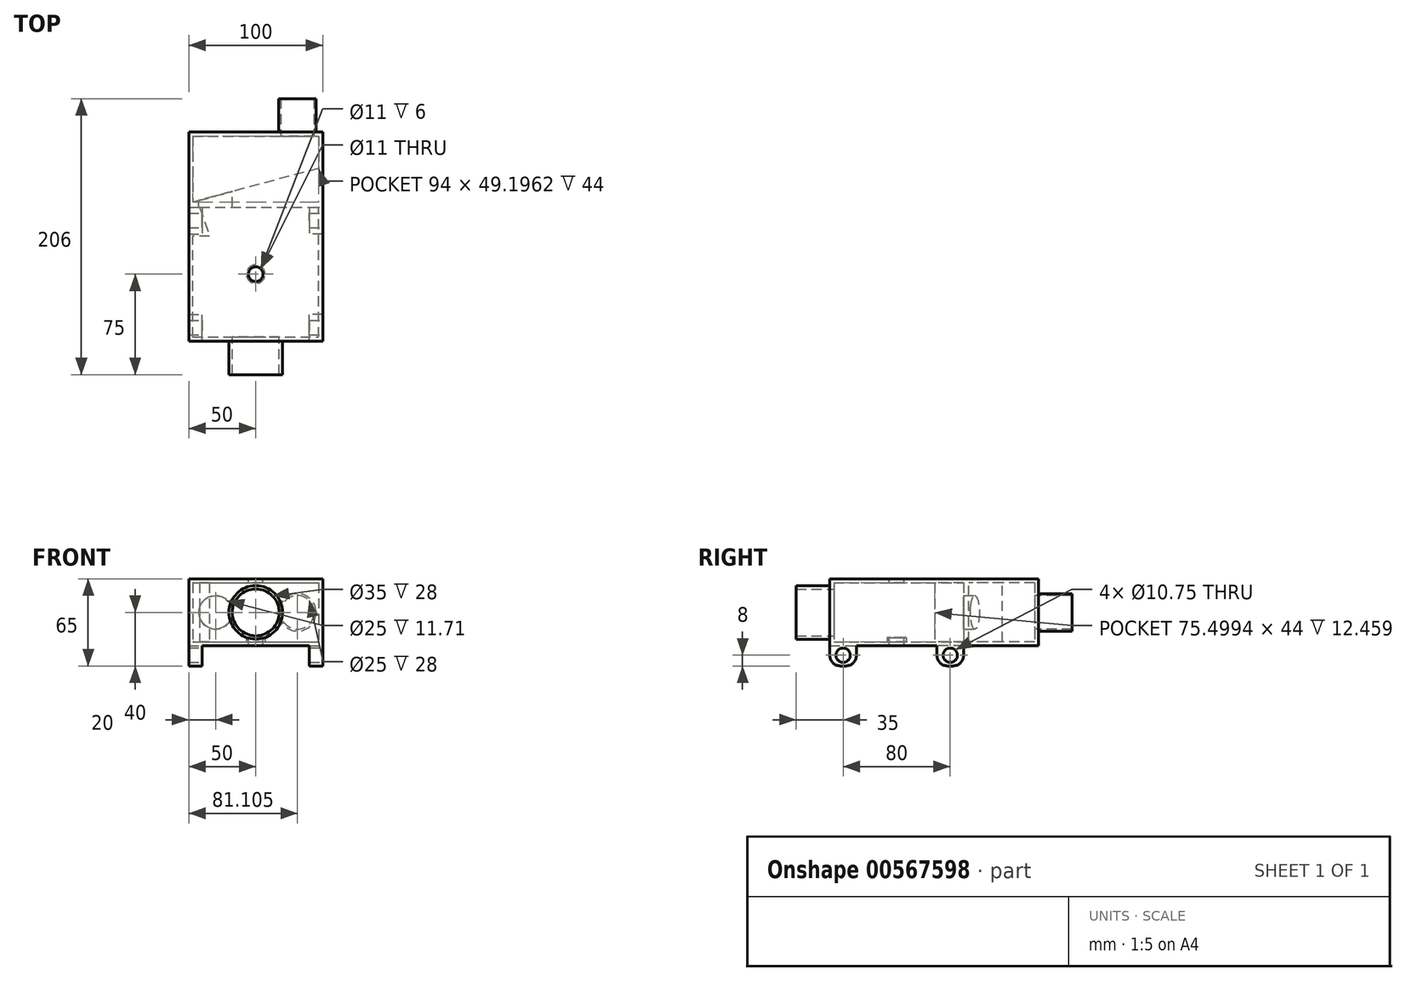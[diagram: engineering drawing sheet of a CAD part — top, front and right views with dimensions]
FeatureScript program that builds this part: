
annotation { "Feature Type Name" : "Feature", "Feature Type Description" : "" }
export const myFeature = defineFeature(function(context is Context, id is Id, definition is map)
    precondition{}
    {
        {
            var Q0;
            Q0=qCreatedBy(makeId("Top.planeOp"),FACE);
            var sketch = newSketch(context, id + "F0", { "sketchPlane" : qUnion([Q0])});
            skLineSegment(sketch, "E0.bottom", {"start": v(-50, -50) * mm, "end": v(50, -50) * mm});
            skLineSegment(sketch, "E0.top", {"start": v(-50, 50) * mm, "end": v(50, 50) * mm});
            skLineSegment(sketch, "E0.left", {"start": v(-50, -50) * mm, "end": v(-50, 50) * mm});
            skLineSegment(sketch, "E0.right", {"start": v(50, -50) * mm, "end": v(50, 50) * mm});
            skPoint(sketch, "E0.middle", {"position": v(0, 0) * mm});
            skSolve(sketch);
        }
        {
            var Q0;
            Q0 = qSketchRegion(id + "F0", true);
            extrude(context, id + "F1", {"entities" : qUnion([Q0]), "depth" : 50 * mm, "offsetDistance" : 25 * mm});
        }
        {
            var Q0;
            Q0=makeQuery(id+"F1.opExtrude","SWEPT_FACE",FACE,{"disambiguationData":[OSD([sQuery(id+"F0.wireOp",EDGE,"E0.top")])]});
            shell(context, id + "F2", {"entities" : qUnion([Q0]), "thickness" : 3 * mm});
        }
        {
            var Q0;
            Q0=makeQuery(id+"F1.opExtrude","CAP_FACE",FACE,{"disambiguationData":[OSD([sQuery(id+"F0.wireOp",EDGE,"E0.bottom"),sQuery(id+"F0.wireOp",EDGE,"E0.top"),sQuery(id+"F0.wireOp",EDGE,"E0.left"),sQuery(id+"F0.wireOp",EDGE,"E0.right")])],"isStart":false});
            var sketch = newSketch(context, id + "F3", { "sketchPlane" : qUnion([Q0])});
            skCircle(sketch, "E1", {"center": v(0, 0) * mm, "radius": 5.5 * mm});
            skSolve(sketch);
        }
        {
            var Q0;
            Q0 = qSketchRegion(id + "F3", true);
            var Q1;
            Q1=makeQuery(id+"F1.opExtrude","CAP_FACE",FACE,{"disambiguationData":[OSD([sQuery(id+"F0.wireOp",EDGE,"E0.bottom"),sQuery(id+"F0.wireOp",EDGE,"E0.top"),sQuery(id+"F0.wireOp",EDGE,"E0.left"),sQuery(id+"F0.wireOp",EDGE,"E0.right")])],"isStart":true});
            extrude(context, id + "F4", {"entities" : qUnion([Q0]), "operationType" : NewBodyOperationType.REMOVE, "endBound" : BoundingType.UP_TO_SURFACE, "oppositeDirection" : true, "depth" : 25 * mm, "endBoundEntityFace" : qUnion([Q1]), "offsetDistance" : 25 * mm});
        }
        {
            var Q0;
            Q0=makeQuery(id+"F1.opExtrude","SWEPT_FACE",FACE,{"disambiguationData":[OSD([sQuery(id+"F0.wireOp",EDGE,"E0.bottom")])]});
            var sketch = newSketch(context, id + "F5", { "sketchPlane" : qUnion([Q0])});
            skCircle(sketch, "E2", {"center": v(0, 25) * mm, "radius": 17.5 * mm});
            skPoint(sketch, "E2.centerSnap0", {"position": v(-50, 25) * mm});
            skPoint(sketch, "E2.centerSnap1", {"position": v(0, 0) * mm});
            skCircle(sketch, "E3", {"center": v(0, 25) * mm, "radius": 20 * mm});
            skSolve(sketch);
        }
        {
            var Q0;
            Q0=makeQuery(id+"F5.imprint","IMPRINT",FACE,{"disambiguationData":[TD([[makeQuery(id+"F5.imprint","IMPRINT",EDGE,{"derivedFrom":sQuery(id+"F5.wireOp",EDGE,"E2")}),-1.0]])]});
            extrude(context, id + "F6", {"entities" : qUnion([Q0]), "operationType" : NewBodyOperationType.ADD, "depth" : 25 * mm, "offsetDistance" : 25 * mm});
        }
        {
            var Q0;
            Q0=makeQuery(id+"F5.imprint","IMPRINT",FACE,{"disambiguationData":[TD([[makeQuery(id+"F5.imprint","IMPRINT",EDGE,{"derivedFrom":sQuery(id+"F5.wireOp",EDGE,"E2")}),1.0]])]});
            extrude(context, id + "F7", {"entities" : qUnion([Q0]), "operationType" : NewBodyOperationType.REMOVE, "endBound" : BoundingType.UP_TO_NEXT, "oppositeDirection" : true, "depth" : 25 * mm, "offsetDistance" : 25 * mm});
        }
        {
            var Q0;
            Q0=makeQuery(id+"F1.opExtrude","CAP_FACE",FACE,{"disambiguationData":[OSD([sQuery(id+"F0.wireOp",EDGE,"E0.bottom"),sQuery(id+"F0.wireOp",EDGE,"E0.top"),sQuery(id+"F0.wireOp",EDGE,"E0.left"),sQuery(id+"F0.wireOp",EDGE,"E0.right")])],"isStart":true});
            var sketch = newSketch(context, id + "F8", { "sketchPlane" : qUnion([Q0])});
            skLineSegment(sketch, "E4.bottom", {"start": v(50, -50) * mm, "end": v(40, -50) * mm});
            skLineSegment(sketch, "E4.top", {"start": v(50, -30) * mm, "end": v(40, -30) * mm});
            skLineSegment(sketch, "E4.left", {"start": v(50, -50) * mm, "end": v(50, -30) * mm});
            skLineSegment(sketch, "E4.right", {"start": v(40, -50) * mm, "end": v(40, -30) * mm});
            skLineSegment(sketch, "E5.bottom", {"start": v(-50, -50) * mm, "end": v(-40, -50) * mm});
            skLineSegment(sketch, "E5.top", {"start": v(-50, -30) * mm, "end": v(-40, -30) * mm});
            skLineSegment(sketch, "E5.left", {"start": v(-50, -50) * mm, "end": v(-50, -30) * mm});
            skLineSegment(sketch, "E5.right", {"start": v(-40, -50) * mm, "end": v(-40, -30) * mm});
            skLineSegment(sketch, "E6.bottom", {"start": v(-50, 50) * mm, "end": v(-40, 50) * mm});
            skLineSegment(sketch, "E6.top", {"start": v(-50, 30) * mm, "end": v(-40, 30) * mm});
            skLineSegment(sketch, "E6.left", {"start": v(-50, 50) * mm, "end": v(-50, 30) * mm});
            skLineSegment(sketch, "E6.right", {"start": v(-40, 50) * mm, "end": v(-40, 30) * mm});
            skLineSegment(sketch, "E7.bottom", {"start": v(50, 50) * mm, "end": v(40, 50) * mm});
            skLineSegment(sketch, "E7.top", {"start": v(50, 30) * mm, "end": v(40, 30) * mm});
            skLineSegment(sketch, "E7.left", {"start": v(50, 50) * mm, "end": v(50, 30) * mm});
            skLineSegment(sketch, "E7.right", {"start": v(40, 50) * mm, "end": v(40, 30) * mm});
            skSolve(sketch);
        }
        {
            var Q0;
            Q0 = qSketchRegion(id + "F8", true);
            extrude(context, id + "F9", {"entities" : qUnion([Q0]), "operationType" : NewBodyOperationType.ADD, "depth" : 15 * mm, "offsetDistance" : 25 * mm});
        }
        {
            var Q0;
            Q0=makeQuery(id+"F9.boolean.opBoolean","MERGE",FACE,{"derivedFrom":[makeQuery(id+"F1.opExtrude","SWEPT_FACE",FACE,{"disambiguationData":[OSD([sQuery(id+"F0.wireOp",EDGE,"E0.right")])]}),makeQuery(id+"F9.opExtrude","SWEPT_FACE",FACE,{"disambiguationData":[OSD([sQuery(id+"F8.wireOp",EDGE,"E4.left")])]}),makeQuery(id+"F9.opExtrude","SWEPT_FACE",FACE,{"disambiguationData":[OSD([sQuery(id+"F8.wireOp",EDGE,"E7.left")])]})]});
            var sketch = newSketch(context, id + "F10", { "sketchPlane" : qUnion([Q0])});
            skCircle(sketch, "E8", {"center": v(40, -7) * mm, "radius": 5.37 * mm});
            skPoint(sketch, "E8.centerSnap0", {"position": v(40, -15) * mm});
            skCircle(sketch, "E9", {"center": v(-40, -7) * mm, "radius": 5.37 * mm});
            skPoint(sketch, "E9.centerSnap0", {"position": v(-40, -15) * mm});
            skSolve(sketch);
        }
        {
            var Q0;
            Q0 = qSketchRegion(id + "F10", true);
            var Q1;
            Q1=makeQuery(id+"F9.boolean.opBoolean","MERGE",FACE,{"derivedFrom":[makeQuery(id+"F1.opExtrude","SWEPT_FACE",FACE,{"disambiguationData":[OSD([sQuery(id+"F0.wireOp",EDGE,"E0.left")])]}),makeQuery(id+"F9.opExtrude","SWEPT_FACE",FACE,{"disambiguationData":[OSD([sQuery(id+"F8.wireOp",EDGE,"E5.left")])]}),makeQuery(id+"F9.opExtrude","SWEPT_FACE",FACE,{"disambiguationData":[OSD([sQuery(id+"F8.wireOp",EDGE,"E6.left")])]})]});
            extrude(context, id + "F11", {"entities" : qUnion([Q0]), "operationType" : NewBodyOperationType.REMOVE, "endBound" : BoundingType.UP_TO_SURFACE, "oppositeDirection" : true, "depth" : 25 * mm, "endBoundEntityFace" : qUnion([Q1]), "offsetDistance" : 25 * mm});
        }
        {
            var Q0;
            Q0=makeQuery(id+"F9.opExtrude","CAP_EDGE",EDGE,{"disambiguationData":[OSD([sQuery(id+"F8.wireOp",EDGE,"E4.top")])],"isStart":false});
            var Q1;
            Q1=makeQuery(id+"F9.opExtrude","CAP_EDGE",EDGE,{"disambiguationData":[OSD([sQuery(id+"F8.wireOp",EDGE,"E4.bottom")])],"isStart":false});
            var Q2;
            Q2=makeQuery(id+"F9.opExtrude","CAP_EDGE",EDGE,{"disambiguationData":[OSD([sQuery(id+"F8.wireOp",EDGE,"E5.bottom")])],"isStart":false});
            var Q3;
            Q3=makeQuery(id+"F9.opExtrude","CAP_EDGE",EDGE,{"disambiguationData":[OSD([sQuery(id+"F8.wireOp",EDGE,"E5.top")])],"isStart":false});
            var Q4;
            Q4=makeQuery(id+"F9.opExtrude","CAP_EDGE",EDGE,{"disambiguationData":[OSD([sQuery(id+"F8.wireOp",EDGE,"E7.bottom")])],"isStart":false});
            var Q5;
            Q5=makeQuery(id+"F9.opExtrude","CAP_EDGE",EDGE,{"disambiguationData":[OSD([sQuery(id+"F8.wireOp",EDGE,"E7.top")])],"isStart":false});
            var Q6;
            Q6=makeQuery(id+"F9.opExtrude","CAP_EDGE",EDGE,{"disambiguationData":[OSD([sQuery(id+"F8.wireOp",EDGE,"E6.bottom")])],"isStart":false});
            var Q7;
            Q7=makeQuery(id+"F9.opExtrude","CAP_EDGE",EDGE,{"disambiguationData":[OSD([sQuery(id+"F8.wireOp",EDGE,"E6.top")])],"isStart":false});
            fillet(context, id + "F12", {"entities" : qUnion([Q0, Q1, Q2, Q3, Q4, Q5, Q6, Q7]), "radius" : 8 * mm, "tangentPropagation" : true, "allowEdgeOverflow" : false});
        }
        {
            var Q0;
            {var subQ0=sQuery(id+"F0.wireOp",EDGE,"E0.right");var subQ1=sQuery(id+"F0.wireOp",EDGE,"E0.left");var subQ2=sQuery(id+"F0.wireOp",EDGE,"E0.top");var subQ3=sQuery(id+"F0.wireOp",EDGE,"E0.bottom");Q0=makeQuery(id+"F2.opShell","OFFSET_FACE",FACE,{"disambiguationData":[OSD([subQ3,subQ2,subQ1,subQ0]),TDD([makeQuery(id+"F1.opExtrude","CAP_FACE",FACE,{"disambiguationData":[OSD([subQ3,subQ2,subQ1,subQ0])],"isStart":true})])]});}
            var sketch = newSketch(context, id + "F13", { "sketchPlane" : qUnion([Q0])});
            skCircle(sketch, "E10", {"center": v(0, 0) * mm, "radius": 7 * mm});
            skSolve(sketch);
        }
        {
            var Q0;
            Q0=makeQuery(id+"F13.imprint","IMPRINT",FACE,{"disambiguationData":[TD([[makeQuery(id+"F13.imprint","IMPRINT",EDGE,{"derivedFrom":sQuery(id+"F13.wireOp",EDGE,"E10")}),1.0]])]});
            extrude(context, id + "F14", {"entities" : qUnion([Q0]), "operationType" : NewBodyOperationType.ADD, "depth" : 3 * mm, "offsetDistance" : 25 * mm});
        }
        {
            var Q0;
            Q0=makeQuery(id+"F9.boolean.opBoolean","MERGE",FACE,{"derivedFrom":[makeQuery(id+"F1.opExtrude","SWEPT_FACE",FACE,{"disambiguationData":[OSD([sQuery(id+"F0.wireOp",EDGE,"E0.top")])]}),makeQuery(id+"F9.opExtrude","SWEPT_FACE",FACE,{"disambiguationData":[OSD([sQuery(id+"F8.wireOp",EDGE,"E4.bottom")])]}),makeQuery(id+"F9.opExtrude","SWEPT_FACE",FACE,{"disambiguationData":[OSD([sQuery(id+"F8.wireOp",EDGE,"E5.bottom")])]})]});
            var sketch = newSketch(context, id + "F15", { "sketchPlane" : qUnion([Q0])});
            skLineSegment(sketch, "E11.bottom", {"start": v(50, 50) * mm, "end": v(-50, 50) * mm});
            skLineSegment(sketch, "E11.top", {"start": v(50, 0) * mm, "end": v(-50, 0) * mm});
            skLineSegment(sketch, "E11.left", {"start": v(50, 50) * mm, "end": v(50, 0) * mm});
            skLineSegment(sketch, "E11.right", {"start": v(-50, 50) * mm, "end": v(-50, 0) * mm});
            skSolve(sketch);
        }
        {
            var Q0;
            Q0 = qSketchRegion(id + "F15", true);
            extrude(context, id + "F16", {"entities" : qUnion([Q0]), "operationType" : NewBodyOperationType.ADD, "depth" : 3 * mm, "offsetDistance" : 25 * mm});
        }
        {
            var Q0;
            Q0=qCreatedBy(makeId("Top.planeOp"),FACE);
            var sketch = newSketch(context, id + "F17", { "sketchPlane" : qUnion([Q0])});
            skLineSegment(sketch, "E12", {"start": v(50, 53) * mm, "end": v(-50, 53) * mm});
            skLineSegment(sketch, "E13", {"start": v(-50, 53) * mm, "end": v(50, 79.8) * mm});
            skLineSegment(sketch, "E14", {"start": v(50, 79.8) * mm, "end": v(50, 53) * mm});
            skSolve(sketch);
        }
        {
            var Q0;
            Q0 = qSketchRegion(id + "F17", true);
            var Q1;
            Q1=makeQuery(id+"F16.boolean.opBoolean","MERGE",FACE,{"derivedFrom":[makeQuery(id+"F1.opExtrude","CAP_FACE",FACE,{"disambiguationData":[OSD([sQuery(id+"F0.wireOp",EDGE,"E0.bottom"),sQuery(id+"F0.wireOp",EDGE,"E0.top"),sQuery(id+"F0.wireOp",EDGE,"E0.left"),sQuery(id+"F0.wireOp",EDGE,"E0.right")])],"isStart":false}),makeQuery(id+"F16.opExtrude","SWEPT_FACE",FACE,{"disambiguationData":[OSD([sQuery(id+"F15.wireOp",EDGE,"E11.bottom")])]})]});
            extrude(context, id + "F18", {"entities" : qUnion([Q0]), "operationType" : NewBodyOperationType.ADD, "endBound" : BoundingType.UP_TO_SURFACE, "depth" : 25 * mm, "endBoundEntityFace" : qUnion([Q1]), "offsetDistance" : 25 * mm});
        }
        {
            var Q0;
            Q0=makeQuery(id+"F16.boolean.opBoolean","MERGE",EDGE,{"derivedFrom":[makeQuery(id+"F1.opExtrude","CAP_EDGE",EDGE,{"disambiguationData":[OSD([sQuery(id+"F0.wireOp",EDGE,"E0.left")])],"isStart":false}),makeQuery(id+"F16.opExtrude","SWEPT_EDGE",EDGE,{"disambiguationData":[OSD([sQuery(id+"F15.wireOp",EDGE,"E11.bottom"),sQuery(id+"F15.wireOp",EDGE,"E11.left")])]})]});
            var Q1;
            {var subQ0=sQuery(id+"F15.wireOp",EDGE,"E11.bottom");Q1=makeQuery(id+"F18.boolean.opBoolean","MERGE",VERTEX,{"derivedFrom":[makeQuery(id+"F16.opExtrude","CAP_VERTEX",VERTEX,{"disambiguationData":[OSD([subQ0,sQuery(id+"F15.wireOp",EDGE,"E11.left")])],"isStart":false}),makeQuery(id+"F18.opExtrude","CAP_VERTEX",VERTEX,{"disambiguationData":[OSD([sQuery(id+"F0.wireOp",EDGE,"E0.bottom"),sQuery(id+"F0.wireOp",EDGE,"E0.top"),sQuery(id+"F0.wireOp",EDGE,"E0.left"),sQuery(id+"F0.wireOp",EDGE,"E0.right"),subQ0,sQuery(id+"F17.wireOp",EDGE,"E12"),sQuery(id+"F17.wireOp",EDGE,"E13")])],"isStart":false})]});}
            cPlane(context, id + "F19", {"entities" : qUnion([Q0, Q1]), "cplaneType" : CPlaneType.CURVE_POINT, "offset" : 25 * mm, "width" : 150 * mm, "height" : 150 * mm});
        }
        {
            var Q0;
            Q0=qCreatedBy(id+"F19.planeOp",FACE);
            var sketch = newSketch(context, id + "F20", { "sketchPlane" : qUnion([Q0])});
            skLineSegment(sketch, "E15.bottom", {"start": v(50, 50) * mm, "end": v(-50, 50) * mm});
            skLineSegment(sketch, "E15.top", {"start": v(50, 0) * mm, "end": v(-50, 0) * mm});
            skLineSegment(sketch, "E15.left", {"start": v(50, 50) * mm, "end": v(50, 0) * mm});
            skLineSegment(sketch, "E15.right", {"start": v(-50, 50) * mm, "end": v(-50, 0) * mm});
            skLineSegment(sketch, "E16.0", {"start": v(-47, 47) * mm, "end": v(-47, 3) * mm});
            skLineSegment(sketch, "E16.1", {"start": v(47, 47) * mm, "end": v(-47, 47) * mm});
            skLineSegment(sketch, "E16.2", {"start": v(47, 47) * mm, "end": v(47, 3) * mm});
            skLineSegment(sketch, "E16.3", {"start": v(47, 3) * mm, "end": v(-47, 3) * mm});
            skSolve(sketch);
        }
        {
            var Q0;
            Q0 = qSketchRegion(id + "F20", true);
            extrude(context, id + "F21", {"entities" : qUnion([Q0]), "operationType" : NewBodyOperationType.ADD, "depth" : 50 * mm, "offsetDistance" : 25 * mm});
        }
        {
            var Q0;
            Q0=makeQuery(id+"F21.opExtrude","CAP_FACE",FACE,{"disambiguationData":[OSD([sQuery(id+"F20.wireOp",EDGE,"E15.bottom"),sQuery(id+"F20.wireOp",EDGE,"E15.top"),sQuery(id+"F20.wireOp",EDGE,"E15.left"),sQuery(id+"F20.wireOp",EDGE,"E15.right"),sQuery(id+"F20.wireOp",EDGE,"E16.0"),sQuery(id+"F20.wireOp",EDGE,"E16.1"),sQuery(id+"F20.wireOp",EDGE,"E16.2"),sQuery(id+"F20.wireOp",EDGE,"E16.3")])],"isStart":false});
            var sketch = newSketch(context, id + "F22", { "sketchPlane" : qUnion([Q0])});
            skCircle(sketch, "E17", {"center": v(30, 25) * mm, "radius": 12.5 * mm});
            skPoint(sketch, "E17.centerSnap0", {"position": v(50, 25) * mm});
            skSolve(sketch);
        }
        {
            var Q0;
            Q0=makeQuery(id+"F22.imprint","IMPRINT",FACE,{"disambiguationData":[TD([[makeQuery(id+"F22.imprint","IMPRINT",EDGE,{"derivedFrom":sQuery(id+"F22.wireOp",EDGE,"E17")}),1.0]])]});
            var Q1;
            Q1=makeQuery(id+"F16.opExtrude","CAP_FACE",FACE,{"disambiguationData":[OSD([sQuery(id+"F15.wireOp",EDGE,"E11.bottom"),sQuery(id+"F15.wireOp",EDGE,"E11.top"),sQuery(id+"F15.wireOp",EDGE,"E11.left"),sQuery(id+"F15.wireOp",EDGE,"E11.right")])],"isStart":true});
            extrude(context, id + "F23", {"entities" : qUnion([Q0]), "operationType" : NewBodyOperationType.REMOVE, "endBound" : BoundingType.UP_TO_SURFACE, "oppositeDirection" : true, "depth" : 25 * mm, "endBoundEntityFace" : qUnion([Q1]), "offsetDistance" : 25 * mm});
        }
        {
            var Q0;
            Q0=makeQuery(id+"F21.opExtrude","CAP_FACE",FACE,{"disambiguationData":[OSD([sQuery(id+"F20.wireOp",EDGE,"E15.bottom"),sQuery(id+"F20.wireOp",EDGE,"E15.top"),sQuery(id+"F20.wireOp",EDGE,"E15.left"),sQuery(id+"F20.wireOp",EDGE,"E15.right"),sQuery(id+"F20.wireOp",EDGE,"E16.0"),sQuery(id+"F20.wireOp",EDGE,"E16.1"),sQuery(id+"F20.wireOp",EDGE,"E16.2"),sQuery(id+"F20.wireOp",EDGE,"E16.3")])],"isStart":false});
            var sketch = newSketch(context, id + "F24", { "sketchPlane" : qUnion([Q0])});
            skLineSegment(sketch, "E18.bottom", {"start": v(50, 0) * mm, "end": v(-50, 0) * mm});
            skLineSegment(sketch, "E18.top", {"start": v(50, 50) * mm, "end": v(-50, 50) * mm});
            skLineSegment(sketch, "E18.left", {"start": v(50, 0) * mm, "end": v(50, 50) * mm});
            skLineSegment(sketch, "E18.right", {"start": v(-50, 0) * mm, "end": v(-50, 50) * mm});
            skSolve(sketch);
        }
        {
            var Q0;
            Q0 = qSketchRegion(id + "F24", true);
            extrude(context, id + "F25", {"entities" : qUnion([Q0]), "operationType" : NewBodyOperationType.ADD, "depth" : 3 * mm, "offsetDistance" : 25 * mm});
        }
        {
            var Q0;
            Q0=makeQuery(id+"F25.opExtrude","CAP_FACE",FACE,{"disambiguationData":[OSD([sQuery(id+"F24.wireOp",EDGE,"E18.bottom"),sQuery(id+"F24.wireOp",EDGE,"E18.top"),sQuery(id+"F24.wireOp",EDGE,"E18.left"),sQuery(id+"F24.wireOp",EDGE,"E18.right")])],"isStart":false});
            var sketch = newSketch(context, id + "F26", { "sketchPlane" : qUnion([Q0])});
            skCircle(sketch, "E19", {"center": v(-31.1, 25) * mm, "radius": 12.5 * mm});
            skPoint(sketch, "E19.centerSnap0", {"position": v(-50, 25) * mm});
            skCircle(sketch, "E20", {"center": v(-31.1, 25) * mm, "radius": 14 * mm});
            skSolve(sketch);
        }
        {
            var Q0;
            Q0=makeQuery(id+"F26.imprint","IMPRINT",FACE,{"disambiguationData":[TD([[makeQuery(id+"F26.imprint","IMPRINT",EDGE,{"derivedFrom":sQuery(id+"F26.wireOp",EDGE,"E19")}),-1.0]])]});
            extrude(context, id + "F27", {"entities" : qUnion([Q0]), "operationType" : NewBodyOperationType.ADD, "depth" : 25 * mm, "offsetDistance" : 25 * mm});
        }
        {
            var Q0;
            Q0=makeQuery(id+"F27.boolean.opBoolean","SPLIT",FACE,{"disambiguationData":[TD([makeQuery(id+"F27.opExtrude","SWEPT_FACE",FACE,{"disambiguationData":[OSD([sQuery(id+"F26.wireOp",EDGE,"E19")])]})])],"derivedFrom":makeQuery(id+"F25.opExtrude","CAP_FACE",FACE,{"disambiguationData":[OSD([sQuery(id+"F24.wireOp",EDGE,"E18.bottom"),sQuery(id+"F24.wireOp",EDGE,"E18.top"),sQuery(id+"F24.wireOp",EDGE,"E18.left"),sQuery(id+"F24.wireOp",EDGE,"E18.right")])],"isStart":false})});
            extrude(context, id + "F28", {"entities" : qUnion([Q0]), "operationType" : NewBodyOperationType.REMOVE, "endBound" : BoundingType.UP_TO_NEXT, "oppositeDirection" : true, "depth" : 25 * mm, "offsetDistance" : 25 * mm});
        }
        {
            var Q0;
            {var subQ0=sQuery(id+"F0.wireOp",EDGE,"E0.right");var subQ1=sQuery(id+"F0.wireOp",EDGE,"E0.left");var subQ2=sQuery(id+"F0.wireOp",EDGE,"E0.top");var subQ3=sQuery(id+"F0.wireOp",EDGE,"E0.bottom");Q0=makeQuery(id+"F2.opShell","OFFSET_FACE",FACE,{"disambiguationData":[OSD([subQ3,subQ2,subQ1,subQ0]),TDD([makeQuery(id+"F1.opExtrude","CAP_FACE",FACE,{"disambiguationData":[OSD([subQ3,subQ2,subQ1,subQ0])],"isStart":true})])]});}
            var sketch = newSketch(context, id + "F29", { "sketchPlane" : qUnion([Q0])});
            skLineSegment(sketch, "E21", {"start": v(-41.8, 50) * mm, "end": v(-34.54, 28.5) * mm});
            skLineSegment(sketch, "E22", {"start": v(-34.54, 28.5) * mm, "end": v(-47, 28.5) * mm});
            skLineSegment(sketch, "E23", {"start": v(-47, 28.5) * mm, "end": v(-47, 50) * mm});
            skLineSegment(sketch, "E24", {"start": v(-47, 50) * mm, "end": v(-41.8, 50) * mm});
            skSolve(sketch);
        }
        {
            var Q0;
            Q0 = qSketchRegion(id + "F29", true);
            extrude(context, id + "F30", {"entities" : qUnion([Q0]), "operationType" : NewBodyOperationType.ADD, "endBound" : BoundingType.UP_TO_NEXT, "depth" : 25 * mm, "offsetDistance" : 25 * mm});
        }
    });
